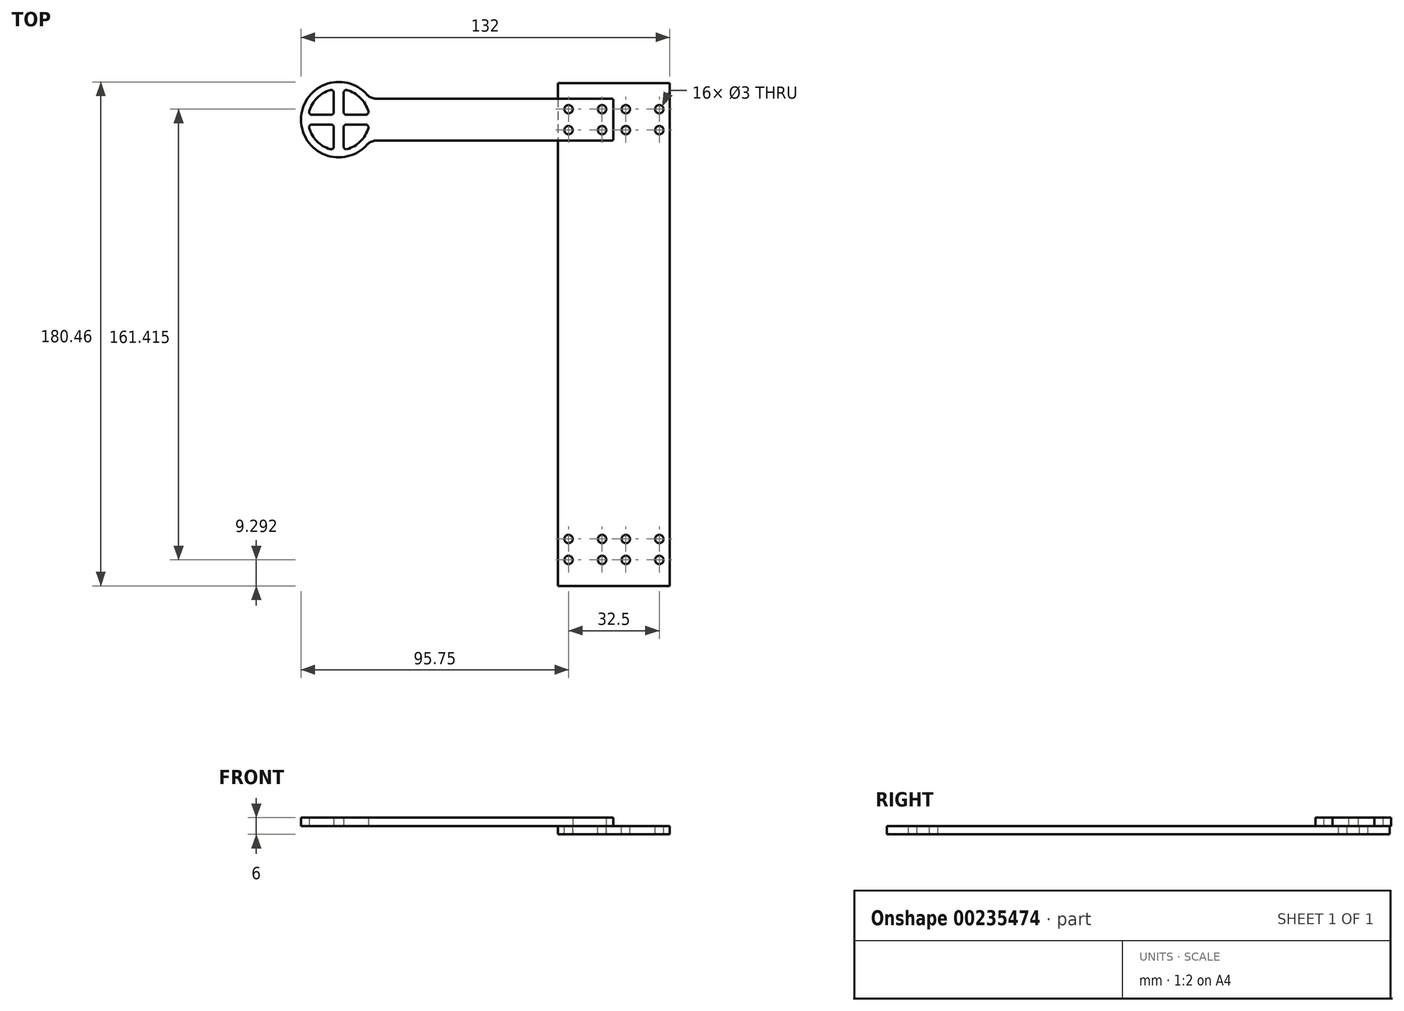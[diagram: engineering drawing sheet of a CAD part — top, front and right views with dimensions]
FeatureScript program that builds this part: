
annotation { "Feature Type Name" : "Feature", "Feature Type Description" : "" }
export const myFeature = defineFeature(function(context is Context, id is Id, definition is map)
    precondition{}
    {
        {
            var Q0;
            Q0=qCreatedBy(makeId("Top.planeOp"),FACE);
            var sketch = newSketch(context, id + "F0", { "sketchPlane" : qUnion([Q0])});
            skCircle(sketch, "E0", {"center": v(0, 0) * mm, "radius": 125 * mm, "construction": true});
            skCircle(sketch, "E1", {"center": v(-98.5, 76.96) * mm, "radius": 70 * mm, "construction": true});
            skCircle(sketch, "E2.MirrorC", {"center": v(98.5, 76.96) * mm, "radius": 70 * mm, "construction": true});
            skCircle(sketch, "E3.MirrorC", {"center": v(98.5, -76.96) * mm, "radius": 70 * mm, "construction": true});
            skCircle(sketch, "E4.MirrorC", {"center": v(-98.5, -76.96) * mm, "radius": 70 * mm, "construction": true});
            skLineSegment(sketch, "E5", {"start": v(-125, 0) * mm, "end": v(0, 0) * mm, "construction": true});
            skLineSegment(sketch, "E6", {"start": v(-98.5, 76.96) * mm, "end": v(0, 0) * mm, "construction": true});
            skSolve(sketch);
        }
        {
            var Q0;
            Q0=qCreatedBy(makeId("Top.planeOp"),FACE);
            var sketch = newSketch(context, id + "F1", { "sketchPlane" : qUnion([Q0])});
            skLineSegment(sketch, "E7", {"start": v(-20, 90) * mm, "end": v(0, 90) * mm});
            skLineSegment(sketch, "E8.MirrorCS", {"start": v(20, 90) * mm, "end": v(0, 90) * mm});
            skLineSegment(sketch, "E9.MirrorCS", {"start": v(-20, -90) * mm, "end": v(0, -90) * mm});
            skLineSegment(sketch, "E10.MirrorCS", {"start": v(20, -90) * mm, "end": v(0, -90) * mm});
            skLineSegment(sketch, "E11", {"start": v(-20, 90) * mm, "end": v(-20, -90) * mm});
            skLineSegment(sketch, "E12", {"start": v(20, -90) * mm, "end": v(20, 90) * mm});
            skSolve(sketch);
        }
        {
            var Q0;
            Q0=makeQuery(id+"F1.imprint","IMPRINT",FACE,{"disambiguationData":[TD([[makeQuery(id+"F1.imprint","IMPRINT",EDGE,{"derivedFrom":sQuery(id+"F1.wireOp",EDGE,"bBznCrm2-QRYQ-iqvx-PbNi-GIdhlFfGiOBs")}),-1.0]])]});
            var Q1;
            Q1=makeQuery(id+"F1.imprint","IMPRINT",FACE,{"disambiguationData":[TD([[makeQuery(id+"F1.imprint","IMPRINT",EDGE,{"derivedFrom":sQuery(id+"F1.wireOp",EDGE,"E7")}),-1.0]])]});
            extrude(context, id + "F2", {"entities" : qUnion([Q0, Q1]), "depth" : 3 * mm});
        }
        {
            var Q0;
            Q0=makeQuery(id+"F2.opExtrude","CAP_FACE",FACE,{"disambiguationData":[OSD([sQuery(id+"F1.wireOp",EDGE,"bBznCrm2-QRYQ-iqvx-PbNi-GIdhlFfGiOBs"),sQuery(id+"F1.wireOp",EDGE,"dxu1rddn-W6Q4-VgDp-YYqR-Kx43ApV7gvQJ"),sQuery(id+"F1.wireOp",EDGE,"E7"),sQuery(id+"F1.wireOp",EDGE,"E8.MirrorCS"),sQuery(id+"F1.wireOp",EDGE,"1dcf4f21-ea1f-4105-97ee-317c8908c3cd1.MirrorCS"),sQuery(id+"F1.wireOp",EDGE,"1dcf4f21-ea1f-4105-97ee-317c8908c3cd2.MirrorCS"),sQuery(id+"F1.wireOp",EDGE,"e060462e-2869-4d07-9b25-fa52a937883f0.MirrorCS"),sQuery(id+"F1.wireOp",EDGE,"e060462e-2869-4d07-9b25-fa52a937883f1.MirrorCS"),sQuery(id+"F1.wireOp",EDGE,"e060462e-2869-4d07-9b25-fa52a937883f2.MirrorCS"),sQuery(id+"F1.wireOp",EDGE,"E9.MirrorCS"),sQuery(id+"F1.wireOp",EDGE,"e060462e-2869-4d07-9b25-fa52a937883f4.MirrorCS"),sQuery(id+"F1.wireOp",EDGE,"E10.MirrorCS")])],"isStart":false});
            var sketch = newSketch(context, id + "F3", { "sketchPlane" : qUnion([Q0])});
            skPoint(sketch, "E13.0", {"position": v(-98.5, 76.96) * mm});
            skArc(sketch, "E14", {"start": v(-88.55, 86.08) * mm, "mid": v(-112, 76.96) * mm, "end": v(-88.55, 67.84) * mm});
            skArc(sketch, "E15", {"start": v(-101.53, 87.53) * mm, "mid": v(-106.28, 84.74) * mm, "end": v(-109.08, 79.98) * mm});
            skLineSegment(sketch, "E16", {"start": v(-100.25, 86.57) * mm, "end": v(-100.25, 79.7) * mm});
            skLineSegment(sketch, "E17", {"start": v(-98.5, 87.96) * mm, "end": v(-98.5, 65.96) * mm, "construction": true});
            skLineSegment(sketch, "E18.MirrorCS", {"start": v(-96.75, 86.57) * mm, "end": v(-96.75, 79.7) * mm});
            skArc(sketch, "E19.trimOffspring", {"start": v(-95.48, 66.38) * mm, "mid": v(-90.72, 69.18) * mm, "end": v(-87.93, 73.93) * mm});
            skLineSegment(sketch, "E20", {"start": v(-108.12, 78.7) * mm, "end": v(-101.25, 78.7) * mm});
            skLineSegment(sketch, "E21", {"start": v(-109.5, 76.96) * mm, "end": v(-87.5, 76.96) * mm, "construction": true});
            skLineSegment(sketch, "E22.MirrorCS", {"start": v(-108.12, 75.2) * mm, "end": v(-101.25, 75.2) * mm});
            skArc(sketch, "E23.trimOffspring", {"start": v(-109.08, 73.93) * mm, "mid": v(-106.28, 69.18) * mm, "end": v(-101.53, 66.38) * mm});
            skArc(sketch, "E24.trimOffspring", {"start": v(-87.93, 79.98) * mm, "mid": v(-90.72, 84.74) * mm, "end": v(-95.48, 87.53) * mm});
            skLineSegment(sketch, "E25.trimOffspring", {"start": v(-96.75, 74.2) * mm, "end": v(-96.75, 67.34) * mm});
            skLineSegment(sketch, "E26.trimOffspring", {"start": v(-95.75, 75.2) * mm, "end": v(-88.89, 75.2) * mm});
            skLineSegment(sketch, "E27.trimOffspring", {"start": v(-100.25, 74.2) * mm, "end": v(-100.25, 67.34) * mm});
            skLineSegment(sketch, "E28.trimOffspring", {"start": v(-95.75, 78.7) * mm, "end": v(-88.89, 78.7) * mm});
            skPoint(sketch, "E29.visualSharp", {"position": v(-109.36, 78.7) * mm});
            skArc(sketch, "E29.filletArc", {"start": v(-109.08, 79.98) * mm, "mid": v(-108.91, 79.1) * mm, "end": v(-108.12, 78.7) * mm});
            skPoint(sketch, "E30.visualSharp", {"position": v(-100.25, 87.82) * mm});
            skArc(sketch, "E30.filletArc", {"start": v(-100.25, 86.57) * mm, "mid": v(-100.65, 87.37) * mm, "end": v(-101.53, 87.53) * mm});
            skPoint(sketch, "E31.visualSharp", {"position": v(-100.25, 78.7) * mm});
            skArc(sketch, "E31.filletArc", {"start": v(-101.25, 78.7) * mm, "mid": v(-100.54, 79) * mm, "end": v(-100.25, 79.7) * mm});
            skPoint(sketch, "E32.visualSharp", {"position": v(-96.75, 78.7) * mm});
            skArc(sketch, "E32.filletArc", {"start": v(-96.75, 79.7) * mm, "mid": v(-96.46, 79) * mm, "end": v(-95.75, 78.7) * mm});
            skPoint(sketch, "E33.visualSharp", {"position": v(-96.75, 87.82) * mm});
            skArc(sketch, "E33.filletArc", {"start": v(-95.48, 87.53) * mm, "mid": v(-96.35, 87.37) * mm, "end": v(-96.75, 86.57) * mm});
            skPoint(sketch, "E34.visualSharp", {"position": v(-87.64, 78.7) * mm});
            skArc(sketch, "E34.filletArc", {"start": v(-88.89, 78.7) * mm, "mid": v(-88.09, 79.1) * mm, "end": v(-87.93, 79.98) * mm});
            skPoint(sketch, "E35.visualSharp", {"position": v(-96.75, 75.2) * mm});
            skArc(sketch, "E35.filletArc", {"start": v(-95.75, 75.2) * mm, "mid": v(-96.46, 74.91) * mm, "end": v(-96.75, 74.2) * mm});
            skPoint(sketch, "E36.visualSharp", {"position": v(-87.64, 75.2) * mm});
            skArc(sketch, "E36.filletArc", {"start": v(-87.93, 73.93) * mm, "mid": v(-88.09, 74.8) * mm, "end": v(-88.89, 75.2) * mm});
            skPoint(sketch, "E37.visualSharp", {"position": v(-96.75, 66.1) * mm});
            skArc(sketch, "E37.filletArc", {"start": v(-96.75, 67.34) * mm, "mid": v(-96.35, 66.54) * mm, "end": v(-95.48, 66.38) * mm});
            skPoint(sketch, "E38.visualSharp", {"position": v(-100.25, 66.1) * mm});
            skArc(sketch, "E38.filletArc", {"start": v(-101.53, 66.38) * mm, "mid": v(-100.65, 66.54) * mm, "end": v(-100.25, 67.34) * mm});
            skPoint(sketch, "E39.visualSharp", {"position": v(-109.36, 75.2) * mm});
            skArc(sketch, "E39.filletArc", {"start": v(-108.12, 75.2) * mm, "mid": v(-108.91, 74.8) * mm, "end": v(-109.08, 73.93) * mm});
            skPoint(sketch, "E40.visualSharp", {"position": v(-100.25, 75.2) * mm});
            skArc(sketch, "E40.filletArc", {"start": v(-100.25, 74.2) * mm, "mid": v(-100.54, 74.91) * mm, "end": v(-101.25, 75.2) * mm});
            skLineSegment(sketch, "E41", {"start": v(-84.86, 84.46) * mm, "end": v(-0.75, 84.46) * mm});
            skLineSegment(sketch, "E42", {"start": v(-98.5, 76.96) * mm, "end": v(0, 76.96) * mm, "construction": true});
            skLineSegment(sketch, "E43.MirrorCS", {"start": v(-84.86, 69.46) * mm, "end": v(-0.75, 69.46) * mm});
            skPoint(sketch, "E44.orphan", {"position": v(0, 69.46) * mm});
            skLineSegment(sketch, "E45", {"start": v(-0.25, 83.96) * mm, "end": v(-0.25, 69.96) * mm});
            skPoint(sketch, "E46.visualSharp", {"position": v(-87.28, 84.46) * mm});
            skArc(sketch, "E46.filletArc", {"start": v(-88.55, 86.08) * mm, "mid": v(-86.88, 84.88) * mm, "end": v(-84.86, 84.46) * mm});
            skPoint(sketch, "E47.visualSharp", {"position": v(-87.28, 69.46) * mm});
            skArc(sketch, "E47.filletArc", {"start": v(-84.86, 69.46) * mm, "mid": v(-86.88, 69.03) * mm, "end": v(-88.55, 67.84) * mm});
            skPoint(sketch, "E48.newPointA", {"position": v(0, 84.46) * mm});
            skArc(sketch, "E48.filletArc", {"start": v(-0.25, 83.96) * mm, "mid": v(-0.4, 84.31) * mm, "end": v(-0.75, 84.46) * mm});
            skArc(sketch, "E49.filletArc", {"start": v(-0.75, 69.46) * mm, "mid": v(-0.4, 69.6) * mm, "end": v(-0.25, 69.96) * mm});
            skCircle(sketch, "E50", {"center": v(-16.25, 80.7) * mm, "radius": 1.5 * mm});
            skCircle(sketch, "E51", {"center": v(-4.25, 80.7) * mm, "radius": 1.5 * mm});
            skCircle(sketch, "E52.MirrorC", {"center": v(-16.25, 73.2) * mm, "radius": 1.5 * mm});
            skCircle(sketch, "E53.MirrorC", {"center": v(-4.25, 73.2) * mm, "radius": 1.5 * mm});
            skSolve(sketch);
        }
        {
            var Q0;
            Q0 = qSketchRegion(id + "F3", true);
            extrude(context, id + "F4", {"entities" : qUnion([Q0]), "operationType" : NewBodyOperationType.ADD, "depth" : 3 * mm});
        }
        {
            var Q0;
            {var subQ46=sQuery(id+"F1.wireOp",EDGE,"E12");var subQ49=sQuery(id+"F1.wireOp",EDGE,"E10.MirrorCS");var subQ50=sQuery(id+"F1.wireOp",EDGE,"E9.MirrorCS");var subQ55=sQuery(id+"F1.wireOp",EDGE,"E8.MirrorCS");var subQ56=sQuery(id+"F1.wireOp",EDGE,"E7");var subQ59=sQuery(id+"F1.wireOp",EDGE,"E11");var subQ60=makeQuery(id+"F2.opExtrude","SWEPT_FACE",FACE,{"disambiguationData":[OSD([subQ59])]});Q0=makeQuery(id+"FsGCkBLtnLEwy8P_1.1.FflXXqpRye77hPx_1.1.F4.boolean.opBoolean","SPLIT",FACE,{"disambiguationData":[TD([subQ60])],"derivedFrom":makeQuery(id+"FsGCkBLtnLEwy8P_1.1.F4.boolean.opBoolean","SPLIT",FACE,{"disambiguationData":[TD([subQ60])],"derivedFrom":makeQuery(id+"FflXXqpRye77hPx_1.1.F4.boolean.opBoolean","SPLIT",FACE,{"disambiguationData":[TD([subQ60])],"derivedFrom":makeQuery(id+"F4.boolean.opBoolean","SPLIT",FACE,{"disambiguationData":[TD([subQ60])],"derivedFrom":makeQuery(id+"F2.opExtrude","CAP_FACE",FACE,{"disambiguationData":[OSD([subQ56,subQ55,subQ50,subQ49,subQ59,subQ46])],"isStart":false})})})})});}
            var sketch = newSketch(context, id + "F5", { "sketchPlane" : qUnion([Q0])});
            skCircle(sketch, "E54.0", {"center": v(-16.25, 80.7) * mm, "radius": 1.5 * mm});
            skCircle(sketch, "E55.0", {"center": v(-4.25, 80.7) * mm, "radius": 1.5 * mm});
            skCircle(sketch, "E56.0", {"center": v(-4.25, 73.2) * mm, "radius": 1.5 * mm});
            skCircle(sketch, "E57.0", {"center": v(-16.25, 73.2) * mm, "radius": 1.5 * mm});
            skCircle(sketch, "E58.0", {"center": v(4.25, 80.7) * mm, "radius": 1.5 * mm});
            skCircle(sketch, "E59.0", {"center": v(16.25, 80.7) * mm, "radius": 1.5 * mm});
            skCircle(sketch, "E60.0", {"center": v(16.25, 73.2) * mm, "radius": 1.5 * mm});
            skCircle(sketch, "E61.0", {"center": v(4.25, 73.2) * mm, "radius": 1.5 * mm});
            skCircle(sketch, "E62.0", {"center": v(4.25, -73.2) * mm, "radius": 1.5 * mm});
            skCircle(sketch, "E63.0", {"center": v(16.25, -73.2) * mm, "radius": 1.5 * mm});
            skCircle(sketch, "E64.0", {"center": v(16.25, -80.7) * mm, "radius": 1.5 * mm});
            skCircle(sketch, "E65.0", {"center": v(4.25, -80.7) * mm, "radius": 1.5 * mm});
            skCircle(sketch, "E66.0", {"center": v(-4.25, -80.7) * mm, "radius": 1.5 * mm});
            skCircle(sketch, "E67.0", {"center": v(-4.25, -73.2) * mm, "radius": 1.5 * mm});
            skCircle(sketch, "E68.0", {"center": v(-16.25, -73.2) * mm, "radius": 1.5 * mm});
            skCircle(sketch, "E69.0", {"center": v(-16.25, -80.7) * mm, "radius": 1.5 * mm});
            skSolve(sketch);
        }
        {
            var Q0;
            Q0 = qSketchRegion(id + "F5", true);
            var Q1;
            Q1=makeQuery(id+"F2.opExtrude","CAP_FACE",FACE,{"disambiguationData":[OSD([sQuery(id+"F1.wireOp",EDGE,"E7"),sQuery(id+"F1.wireOp",EDGE,"E8.MirrorCS"),sQuery(id+"F1.wireOp",EDGE,"E9.MirrorCS"),sQuery(id+"F1.wireOp",EDGE,"E10.MirrorCS"),sQuery(id+"F1.wireOp",EDGE,"E11"),sQuery(id+"F1.wireOp",EDGE,"E12")])],"isStart":true});
            extrude(context, id + "F6", {"entities" : qUnion([Q0]), "operationType" : NewBodyOperationType.REMOVE, "endBound" : BoundingType.UP_TO_SURFACE, "oppositeDirection" : true, "endBoundEntityFace" : qUnion([Q1]), "depth" : 25 * mm});
        }
    });
